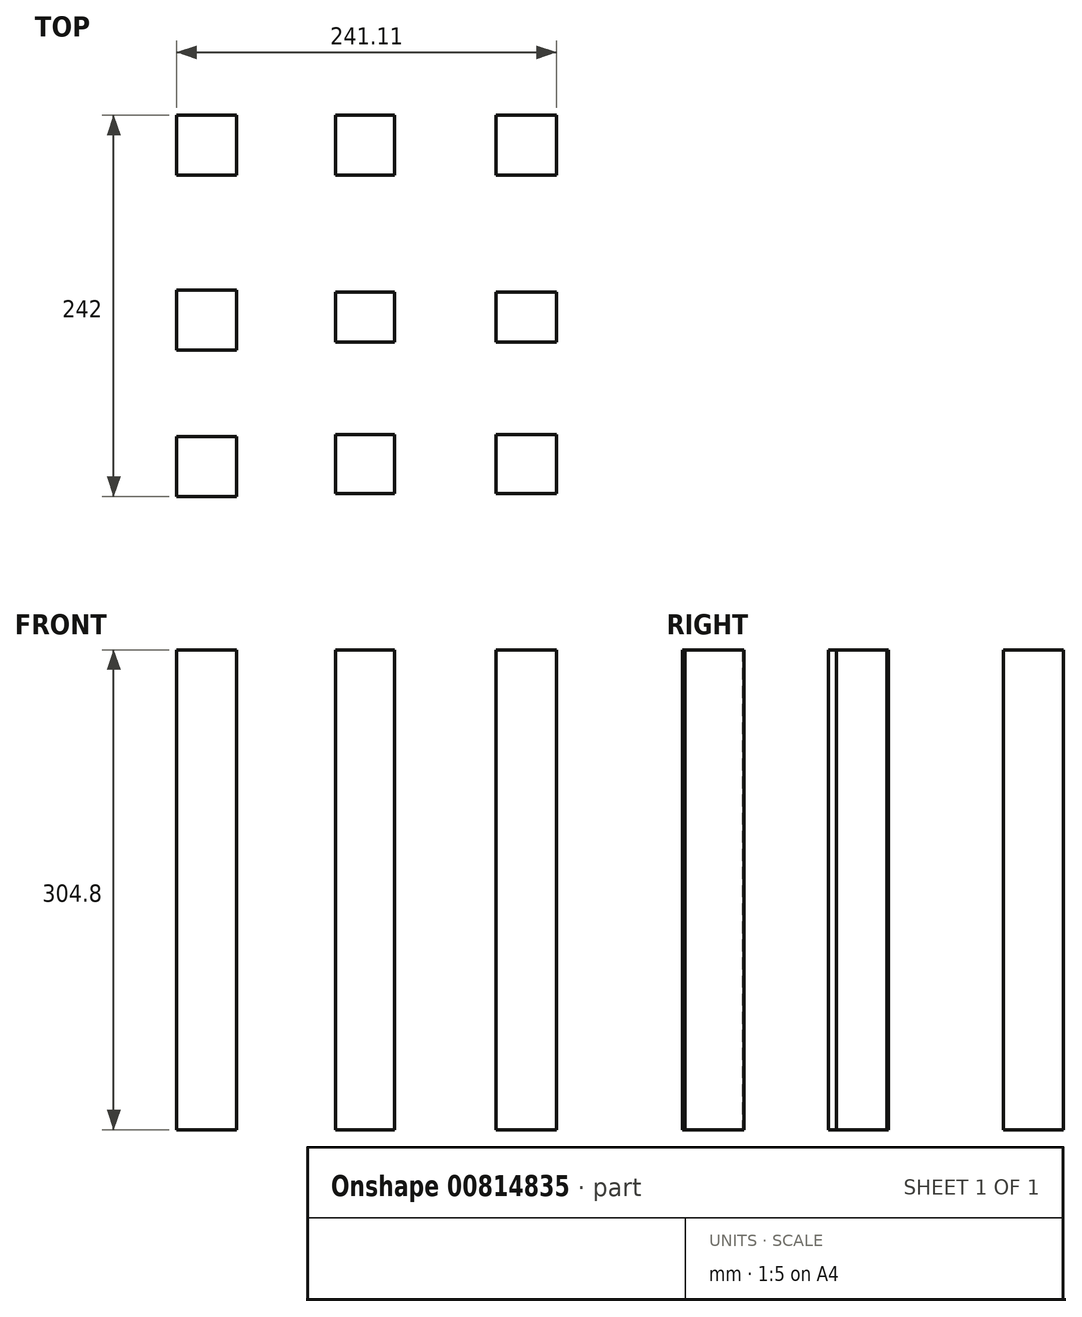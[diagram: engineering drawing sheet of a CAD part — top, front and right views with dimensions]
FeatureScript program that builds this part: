
annotation { "Feature Type Name" : "Feature", "Feature Type Description" : "" }
export const myFeature = defineFeature(function(context is Context, id is Id, definition is map)
    precondition{}
    {
        {
            var Q0;
            Q0=qCreatedBy(makeId("Top.planeOp"),FACE);
            var sketch = newSketch(context, id + "F0", { "sketchPlane" : qUnion([Q0])});
            skLineSegment(sketch, "E0.bottom", {"start": v(-255.49, 202.22) * mm, "end": v(49.31, 202.22) * mm});
            skLineSegment(sketch, "E0.top", {"start": v(-255.49, -102.58) * mm, "end": v(49.31, -102.58) * mm});
            skLineSegment(sketch, "E0.left", {"start": v(-255.49, 202.22) * mm, "end": v(-255.49, -102.58) * mm});
            skLineSegment(sketch, "E0.right", {"start": v(49.31, 202.22) * mm, "end": v(49.31, -102.58) * mm});
            skSolve(sketch);
        }
        {
            var Q0;
            Q0=makeQuery(id+"F0.imprint","IMPRINT",FACE,{"disambiguationData":[TD([[makeQuery(id+"F0.imprint","IMPRINT",EDGE,{"derivedFrom":sQuery(id+"F0.wireOp",EDGE,"E0.bottom")}),-1.0]])]});
            var sketch = newSketch(context, id + "F1", { "sketchPlane" : qUnion([Q0])});
            skLineSegment(sketch, "E1.bottom", {"start": v(-233.44, 187.73) * mm, "end": v(-195.34, 187.73) * mm});
            skLineSegment(sketch, "E1.top", {"start": v(-233.44, 149.63) * mm, "end": v(-195.34, 149.63) * mm});
            skLineSegment(sketch, "E1.left", {"start": v(-233.44, 187.73) * mm, "end": v(-233.44, 149.63) * mm});
            skLineSegment(sketch, "E1.right", {"start": v(-195.34, 187.73) * mm, "end": v(-195.34, 149.63) * mm});
            skLineSegment(sketch, "E2.bottom", {"start": v(-233.44, 76.6) * mm, "end": v(-195.34, 76.6) * mm});
            skLineSegment(sketch, "E2.top", {"start": v(-233.44, 38.5) * mm, "end": v(-195.34, 38.5) * mm});
            skLineSegment(sketch, "E2.left", {"start": v(-233.44, 76.6) * mm, "end": v(-233.44, 38.5) * mm});
            skLineSegment(sketch, "E2.right", {"start": v(-195.34, 76.6) * mm, "end": v(-195.34, 38.5) * mm});
            skLineSegment(sketch, "E3.bottom", {"start": v(-233.44, -16.17) * mm, "end": v(-195.34, -16.17) * mm});
            skLineSegment(sketch, "E3.top", {"start": v(-233.44, -54.27) * mm, "end": v(-195.34, -54.27) * mm});
            skLineSegment(sketch, "E3.left", {"start": v(-233.44, -16.17) * mm, "end": v(-233.44, -54.27) * mm});
            skLineSegment(sketch, "E3.right", {"start": v(-195.34, -16.17) * mm, "end": v(-195.34, -54.27) * mm});
            skSolve(sketch);
        }
        {
            var Q0;
            Q0 = qSketchRegion(id + "F1", true);
            extrude(context, id + "F2", {"entities" : qUnion([Q0]), "depth" : 304.8 * mm, "offsetDistance" : 25.4 * mm});
        }
        {
            var Q0;
            Q0=makeQuery(id+"F2.opExtrude","CAP_FACE",FACE,{"disambiguationData":[OSD([sQuery(id+"F1.wireOp",EDGE,"E1.bottom"),sQuery(id+"F1.wireOp",EDGE,"E1.top"),sQuery(id+"F1.wireOp",EDGE,"E1.left"),sQuery(id+"F1.wireOp",EDGE,"E1.right")])],"isStart":false});
            var sketch = newSketch(context, id + "F3", { "sketchPlane" : qUnion([Q0])});
            skLineSegment(sketch, "E4.bottom", {"start": v(-132.63, 187.73) * mm, "end": v(-95, 187.73) * mm});
            skLineSegment(sketch, "E4.top", {"start": v(-132.63, 149.63) * mm, "end": v(-95, 149.63) * mm});
            skLineSegment(sketch, "E4.left", {"start": v(-132.63, 187.73) * mm, "end": v(-132.63, 149.63) * mm});
            skLineSegment(sketch, "E4.right", {"start": v(-95, 187.73) * mm, "end": v(-95, 149.63) * mm});
            skLineSegment(sketch, "E5.bottom", {"start": v(-30.6, 187.73) * mm, "end": v(7.67, 187.73) * mm});
            skLineSegment(sketch, "E5.top", {"start": v(-30.6, 149.63) * mm, "end": v(7.67, 149.63) * mm});
            skLineSegment(sketch, "E5.left", {"start": v(-30.6, 187.73) * mm, "end": v(-30.6, 149.63) * mm});
            skLineSegment(sketch, "E5.right", {"start": v(7.67, 187.73) * mm, "end": v(7.67, 149.63) * mm});
            skLineSegment(sketch, "E6.bottom", {"start": v(-132.63, 75.51) * mm, "end": v(-95, 75.51) * mm});
            skLineSegment(sketch, "E6.top", {"start": v(-132.63, 43.63) * mm, "end": v(-95, 43.63) * mm});
            skLineSegment(sketch, "E6.left", {"start": v(-132.63, 75.51) * mm, "end": v(-132.63, 43.63) * mm});
            skLineSegment(sketch, "E6.right", {"start": v(-95, 75.51) * mm, "end": v(-95, 43.63) * mm});
            skLineSegment(sketch, "E7.bottom", {"start": v(-30.6, 75.51) * mm, "end": v(7.67, 75.51) * mm});
            skLineSegment(sketch, "E7.top", {"start": v(-30.6, 43.63) * mm, "end": v(7.67, 43.63) * mm});
            skLineSegment(sketch, "E7.left", {"start": v(-30.6, 75.51) * mm, "end": v(-30.6, 43.63) * mm});
            skLineSegment(sketch, "E7.right", {"start": v(7.67, 75.51) * mm, "end": v(7.67, 43.63) * mm});
            skLineSegment(sketch, "E8.bottom", {"start": v(7.67, -15.04) * mm, "end": v(-30.6, -15.04) * mm});
            skLineSegment(sketch, "E8.top", {"start": v(7.67, -52.67) * mm, "end": v(-30.6, -52.67) * mm});
            skLineSegment(sketch, "E8.left", {"start": v(7.67, -15.04) * mm, "end": v(7.67, -52.67) * mm});
            skLineSegment(sketch, "E8.right", {"start": v(-30.6, -15.04) * mm, "end": v(-30.6, -52.67) * mm});
            skLineSegment(sketch, "E9.bottom", {"start": v(-95, -15.04) * mm, "end": v(-132.63, -15.04) * mm});
            skLineSegment(sketch, "E9.top", {"start": v(-95, -52.67) * mm, "end": v(-132.63, -52.67) * mm});
            skLineSegment(sketch, "E9.left", {"start": v(-95, -15.04) * mm, "end": v(-95, -52.67) * mm});
            skLineSegment(sketch, "E9.right", {"start": v(-132.63, -15.04) * mm, "end": v(-132.63, -52.67) * mm});
            skSolve(sketch);
        }
        {
            var Q0;
            Q0 = qSketchRegion(id + "F3", true);
            extrude(context, id + "F4", {"entities" : qUnion([Q0]), "oppositeDirection" : true, "depth" : 304.8 * mm, "offsetDistance" : 25.4 * mm});
        }
    });
